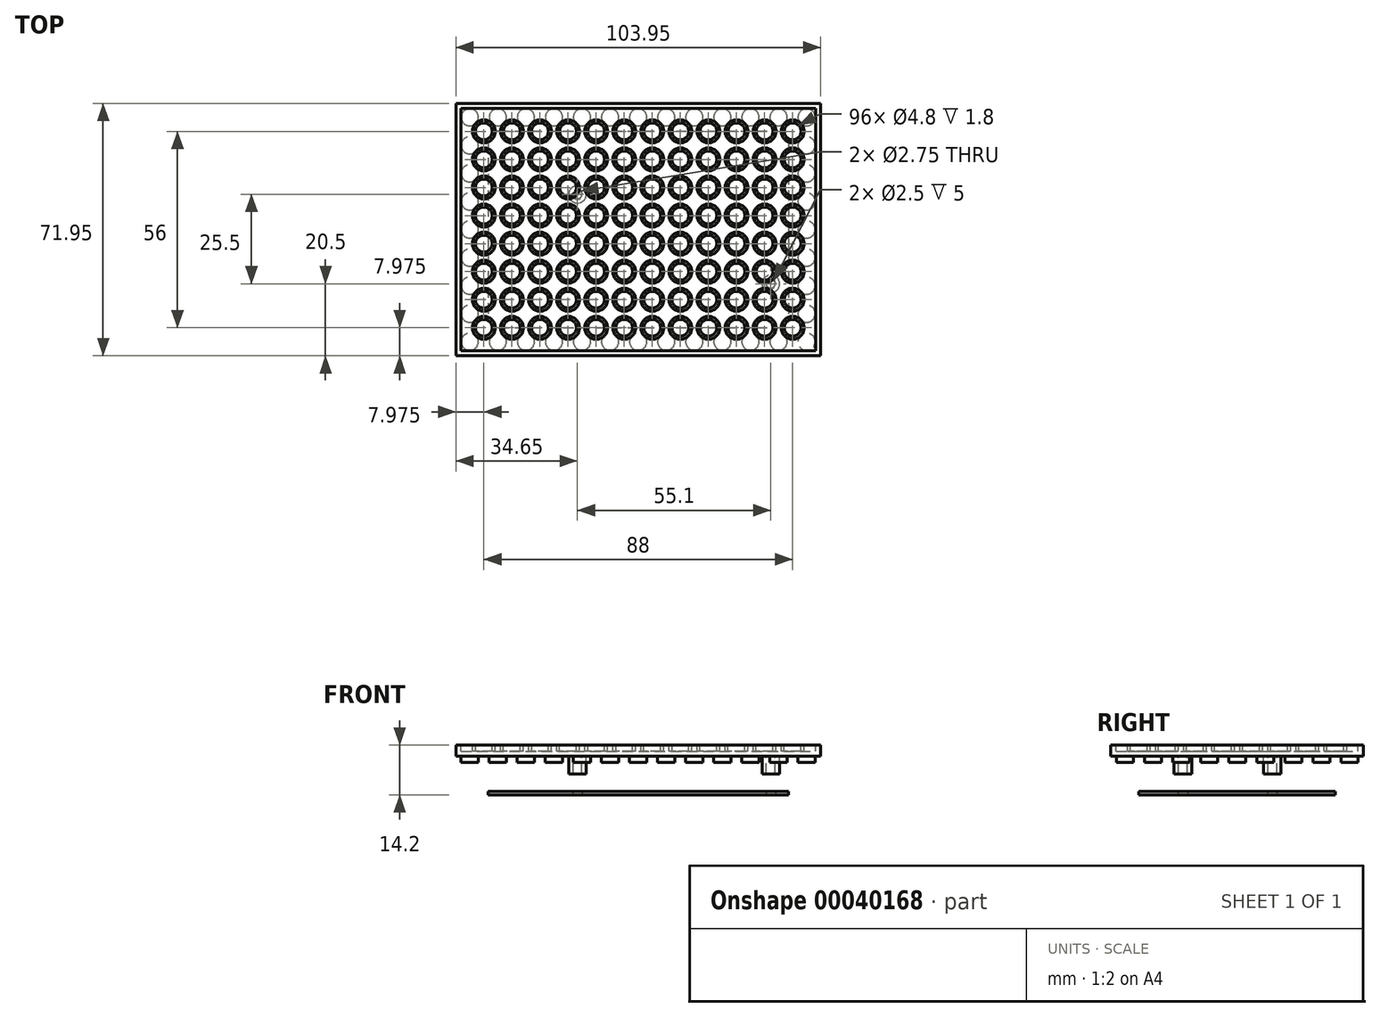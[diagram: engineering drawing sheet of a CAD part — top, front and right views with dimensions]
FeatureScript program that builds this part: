
annotation { "Feature Type Name" : "Feature", "Feature Type Description" : "" }
export const myFeature = defineFeature(function(context is Context, id is Id, definition is map)
    precondition{}
    {
        {
            var Q0;
            Q0=qCreatedBy(makeId("Top.planeOp"),FACE);
            var sketch = newSketch(context, id + "F0", { "sketchPlane" : qUnion([Q0])});
            skLineSegment(sketch, "E0.bottom", {"start": v(0, 0) * mm, "end": v(-103.95, 0) * mm});
            skLineSegment(sketch, "E0.top", {"start": v(0, 71.95) * mm, "end": v(-103.95, 71.95) * mm});
            skLineSegment(sketch, "E0.left", {"start": v(0, 0) * mm, "end": v(0, 71.95) * mm});
            skLineSegment(sketch, "E0.right", {"start": v(-103.95, 0) * mm, "end": v(-103.95, 71.95) * mm});
            skSolve(sketch);
        }
        {
            var Q0;
            Q0=makeQuery(id+"F0.imprint","IMPRINT",FACE,{"disambiguationData":[TD([[makeQuery(id+"F0.imprint","IMPRINT",EDGE,{"derivedFrom":sQuery(id+"F0.wireOp",EDGE,"E0.bottom")}),-1.0]])]});
            extrude(context, id + "F1", {"entities" : qUnion([Q0]), "oppositeDirection" : true, "depth" : 3.2 * mm});
        }
        {
            var Q0;
            Q0=qCreatedBy(makeId("Top.planeOp"),FACE);
            var sketch = newSketch(context, id + "F2", { "sketchPlane" : qUnion([Q0])});
            skLineSegment(sketch, "E1.bottom", {"start": v(-102.47, 1.47) * mm, "end": v(-1.47, 1.48) * mm});
            skLineSegment(sketch, "E1.top", {"start": v(-102.48, 70.47) * mm, "end": v(-1.48, 70.47) * mm});
            skLineSegment(sketch, "E1.left", {"start": v(-102.47, 1.47) * mm, "end": v(-102.48, 70.47) * mm});
            skLineSegment(sketch, "E1.right", {"start": v(-1.47, 1.48) * mm, "end": v(-1.48, 70.47) * mm});
            skCircle(sketch, "E2", {"center": v(-7.97, 7.98) * mm, "radius": 3.25 * mm});
            skLineSegment(sketch, "E3", {"start": v(-7.97, 7.98) * mm, "end": v(-7.98, 45.54) * mm, "construction": true});
            skCircle(sketch, "E4.0.1.0", {"center": v(-7.97, 15.98) * mm, "radius": 3.25 * mm});
            skCircle(sketch, "E4.0.2.0", {"center": v(-7.97, 23.98) * mm, "radius": 3.25 * mm});
            skCircle(sketch, "E4.0.3.0", {"center": v(-7.97, 31.98) * mm, "radius": 3.25 * mm});
            skCircle(sketch, "E4.0.4.0", {"center": v(-7.97, 39.98) * mm, "radius": 3.25 * mm});
            skCircle(sketch, "E4.0.5.0", {"center": v(-7.97, 47.98) * mm, "radius": 3.25 * mm});
            skCircle(sketch, "E4.0.6.0", {"center": v(-7.97, 55.98) * mm, "radius": 3.25 * mm});
            skCircle(sketch, "E4.0.7.0", {"center": v(-7.97, 63.98) * mm, "radius": 3.25 * mm});
            skCircle(sketch, "E4.1.0.0", {"center": v(-15.97, 7.98) * mm, "radius": 3.25 * mm});
            skCircle(sketch, "E4.1.1.0", {"center": v(-15.97, 15.98) * mm, "radius": 3.25 * mm});
            skCircle(sketch, "E4.1.2.0", {"center": v(-15.97, 23.98) * mm, "radius": 3.25 * mm});
            skCircle(sketch, "E4.1.3.0", {"center": v(-15.97, 31.98) * mm, "radius": 3.25 * mm});
            skCircle(sketch, "E4.1.4.0", {"center": v(-15.97, 39.98) * mm, "radius": 3.25 * mm});
            skCircle(sketch, "E4.1.5.0", {"center": v(-15.97, 47.98) * mm, "radius": 3.25 * mm});
            skCircle(sketch, "E4.1.6.0", {"center": v(-15.97, 55.98) * mm, "radius": 3.25 * mm});
            skCircle(sketch, "E4.1.7.0", {"center": v(-15.97, 63.98) * mm, "radius": 3.25 * mm});
            skCircle(sketch, "E4.2.0.0", {"center": v(-23.97, 7.98) * mm, "radius": 3.25 * mm});
            skCircle(sketch, "E4.2.1.0", {"center": v(-23.97, 15.98) * mm, "radius": 3.25 * mm});
            skCircle(sketch, "E4.2.2.0", {"center": v(-23.97, 23.98) * mm, "radius": 3.25 * mm});
            skCircle(sketch, "E4.2.3.0", {"center": v(-23.97, 31.98) * mm, "radius": 3.25 * mm});
            skCircle(sketch, "E4.2.4.0", {"center": v(-23.97, 39.98) * mm, "radius": 3.25 * mm});
            skCircle(sketch, "E4.2.5.0", {"center": v(-23.97, 47.98) * mm, "radius": 3.25 * mm});
            skCircle(sketch, "E4.2.6.0", {"center": v(-23.97, 55.98) * mm, "radius": 3.25 * mm});
            skCircle(sketch, "E4.2.7.0", {"center": v(-23.97, 63.98) * mm, "radius": 3.25 * mm});
            skCircle(sketch, "E4.3.0.0", {"center": v(-31.97, 7.98) * mm, "radius": 3.25 * mm});
            skCircle(sketch, "E4.3.1.0", {"center": v(-31.97, 15.98) * mm, "radius": 3.25 * mm});
            skCircle(sketch, "E4.3.2.0", {"center": v(-31.97, 23.98) * mm, "radius": 3.25 * mm});
            skCircle(sketch, "E4.3.3.0", {"center": v(-31.97, 31.98) * mm, "radius": 3.25 * mm});
            skCircle(sketch, "E4.3.4.0", {"center": v(-31.97, 39.98) * mm, "radius": 3.25 * mm});
            skCircle(sketch, "E4.3.5.0", {"center": v(-31.97, 47.98) * mm, "radius": 3.25 * mm});
            skCircle(sketch, "E4.3.6.0", {"center": v(-31.97, 55.98) * mm, "radius": 3.25 * mm});
            skCircle(sketch, "E4.3.7.0", {"center": v(-31.97, 63.98) * mm, "radius": 3.25 * mm});
            skCircle(sketch, "E4.4.0.0", {"center": v(-39.97, 7.98) * mm, "radius": 3.25 * mm});
            skCircle(sketch, "E4.4.1.0", {"center": v(-39.97, 15.98) * mm, "radius": 3.25 * mm});
            skCircle(sketch, "E4.4.2.0", {"center": v(-39.97, 23.98) * mm, "radius": 3.25 * mm});
            skCircle(sketch, "E4.4.3.0", {"center": v(-39.97, 31.98) * mm, "radius": 3.25 * mm});
            skCircle(sketch, "E4.4.4.0", {"center": v(-39.97, 39.98) * mm, "radius": 3.25 * mm});
            skCircle(sketch, "E4.4.5.0", {"center": v(-39.97, 47.98) * mm, "radius": 3.25 * mm});
            skCircle(sketch, "E4.4.6.0", {"center": v(-39.97, 55.98) * mm, "radius": 3.25 * mm});
            skCircle(sketch, "E4.4.7.0", {"center": v(-39.97, 63.98) * mm, "radius": 3.25 * mm});
            skCircle(sketch, "E4.5.0.0", {"center": v(-47.97, 7.98) * mm, "radius": 3.25 * mm});
            skCircle(sketch, "E4.5.1.0", {"center": v(-47.97, 15.98) * mm, "radius": 3.25 * mm});
            skCircle(sketch, "E4.5.2.0", {"center": v(-47.97, 23.98) * mm, "radius": 3.25 * mm});
            skCircle(sketch, "E4.5.3.0", {"center": v(-47.97, 31.98) * mm, "radius": 3.25 * mm});
            skCircle(sketch, "E4.5.4.0", {"center": v(-47.97, 39.98) * mm, "radius": 3.25 * mm});
            skCircle(sketch, "E4.5.5.0", {"center": v(-47.97, 47.98) * mm, "radius": 3.25 * mm});
            skCircle(sketch, "E4.5.6.0", {"center": v(-47.97, 55.98) * mm, "radius": 3.25 * mm});
            skCircle(sketch, "E4.5.7.0", {"center": v(-47.97, 63.98) * mm, "radius": 3.25 * mm});
            skCircle(sketch, "E4.6.0.0", {"center": v(-55.97, 7.98) * mm, "radius": 3.25 * mm});
            skCircle(sketch, "E4.6.1.0", {"center": v(-55.97, 15.98) * mm, "radius": 3.25 * mm});
            skCircle(sketch, "E4.6.2.0", {"center": v(-55.97, 23.98) * mm, "radius": 3.25 * mm});
            skCircle(sketch, "E4.6.3.0", {"center": v(-55.97, 31.98) * mm, "radius": 3.25 * mm});
            skCircle(sketch, "E4.6.4.0", {"center": v(-55.97, 39.98) * mm, "radius": 3.25 * mm});
            skCircle(sketch, "E4.6.5.0", {"center": v(-55.97, 47.98) * mm, "radius": 3.25 * mm});
            skCircle(sketch, "E4.6.6.0", {"center": v(-55.97, 55.98) * mm, "radius": 3.25 * mm});
            skCircle(sketch, "E4.6.7.0", {"center": v(-55.97, 63.98) * mm, "radius": 3.25 * mm});
            skCircle(sketch, "E4.7.0.0", {"center": v(-63.98, 7.98) * mm, "radius": 3.25 * mm});
            skCircle(sketch, "E4.7.1.0", {"center": v(-63.98, 15.98) * mm, "radius": 3.25 * mm});
            skCircle(sketch, "E4.7.2.0", {"center": v(-63.98, 23.98) * mm, "radius": 3.25 * mm});
            skCircle(sketch, "E4.7.3.0", {"center": v(-63.98, 31.98) * mm, "radius": 3.25 * mm});
            skCircle(sketch, "E4.7.4.0", {"center": v(-63.98, 39.98) * mm, "radius": 3.25 * mm});
            skCircle(sketch, "E4.7.5.0", {"center": v(-63.98, 47.98) * mm, "radius": 3.25 * mm});
            skCircle(sketch, "E4.7.6.0", {"center": v(-63.98, 55.98) * mm, "radius": 3.25 * mm});
            skCircle(sketch, "E4.7.7.0", {"center": v(-63.98, 63.98) * mm, "radius": 3.25 * mm});
            skCircle(sketch, "E4.8.0.0", {"center": v(-71.97, 7.98) * mm, "radius": 3.25 * mm});
            skCircle(sketch, "E4.8.1.0", {"center": v(-71.97, 15.98) * mm, "radius": 3.25 * mm});
            skCircle(sketch, "E4.8.2.0", {"center": v(-71.97, 23.98) * mm, "radius": 3.25 * mm});
            skCircle(sketch, "E4.8.3.0", {"center": v(-71.97, 31.98) * mm, "radius": 3.25 * mm});
            skCircle(sketch, "E4.8.4.0", {"center": v(-71.97, 39.98) * mm, "radius": 3.25 * mm});
            skCircle(sketch, "E4.8.5.0", {"center": v(-71.97, 47.98) * mm, "radius": 3.25 * mm});
            skCircle(sketch, "E4.8.6.0", {"center": v(-71.97, 55.98) * mm, "radius": 3.25 * mm});
            skCircle(sketch, "E4.8.7.0", {"center": v(-71.97, 63.98) * mm, "radius": 3.25 * mm});
            skCircle(sketch, "E4.9.0.0", {"center": v(-79.98, 7.98) * mm, "radius": 3.25 * mm});
            skCircle(sketch, "E4.9.1.0", {"center": v(-79.98, 15.98) * mm, "radius": 3.25 * mm});
            skCircle(sketch, "E4.9.2.0", {"center": v(-79.98, 23.98) * mm, "radius": 3.25 * mm});
            skCircle(sketch, "E4.9.3.0", {"center": v(-79.98, 31.98) * mm, "radius": 3.25 * mm});
            skCircle(sketch, "E4.9.4.0", {"center": v(-79.98, 39.98) * mm, "radius": 3.25 * mm});
            skCircle(sketch, "E4.9.5.0", {"center": v(-79.98, 47.98) * mm, "radius": 3.25 * mm});
            skCircle(sketch, "E4.9.6.0", {"center": v(-79.98, 55.98) * mm, "radius": 3.25 * mm});
            skCircle(sketch, "E4.9.7.0", {"center": v(-79.98, 63.98) * mm, "radius": 3.25 * mm});
            skCircle(sketch, "E4.10.0.0", {"center": v(-87.97, 7.98) * mm, "radius": 3.25 * mm});
            skCircle(sketch, "E4.10.1.0", {"center": v(-87.97, 15.98) * mm, "radius": 3.25 * mm});
            skCircle(sketch, "E4.10.2.0", {"center": v(-87.97, 23.98) * mm, "radius": 3.25 * mm});
            skCircle(sketch, "E4.10.3.0", {"center": v(-87.97, 31.98) * mm, "radius": 3.25 * mm});
            skCircle(sketch, "E4.10.4.0", {"center": v(-87.97, 39.98) * mm, "radius": 3.25 * mm});
            skCircle(sketch, "E4.10.5.0", {"center": v(-87.97, 47.98) * mm, "radius": 3.25 * mm});
            skCircle(sketch, "E4.10.6.0", {"center": v(-87.97, 55.98) * mm, "radius": 3.25 * mm});
            skCircle(sketch, "E4.10.7.0", {"center": v(-87.97, 63.98) * mm, "radius": 3.25 * mm});
            skCircle(sketch, "E4.11.0.0", {"center": v(-95.97, 7.98) * mm, "radius": 3.25 * mm});
            skCircle(sketch, "E4.11.1.0", {"center": v(-95.97, 15.98) * mm, "radius": 3.25 * mm});
            skCircle(sketch, "E4.11.2.0", {"center": v(-95.97, 23.98) * mm, "radius": 3.25 * mm});
            skCircle(sketch, "E4.11.3.0", {"center": v(-95.97, 31.98) * mm, "radius": 3.25 * mm});
            skCircle(sketch, "E4.11.4.0", {"center": v(-95.97, 39.98) * mm, "radius": 3.25 * mm});
            skCircle(sketch, "E4.11.5.0", {"center": v(-95.97, 47.98) * mm, "radius": 3.25 * mm});
            skCircle(sketch, "E4.11.6.0", {"center": v(-95.97, 55.98) * mm, "radius": 3.25 * mm});
            skCircle(sketch, "E4.11.7.0", {"center": v(-95.97, 63.98) * mm, "radius": 3.25 * mm});
            skLineSegment(sketch, "E4.direction1", {"start": v(-7.97, 7.98) * mm, "end": v(-15.97, 7.98) * mm, "construction": true});
            skLineSegment(sketch, "E4.direction2", {"start": v(-7.97, 7.98) * mm, "end": v(-7.97, 15.98) * mm, "construction": true});
            skSolve(sketch);
        }
        {
            var Q0;
            Q0=qCreatedBy(makeId("Top.planeOp"),FACE);
            var sketch = newSketch(context, id + "F3", { "sketchPlane" : qUnion([Q0])});
            skCircle(sketch, "E5", {"center": v(-7.97, 7.97) * mm, "radius": 2.4 * mm});
            skLineSegment(sketch, "E6", {"start": v(-7.97, 7.97) * mm, "end": v(-7.97, 10.16) * mm, "construction": true});
            skCircle(sketch, "E7.0.1.0", {"center": v(-7.97, 15.97) * mm, "radius": 2.4 * mm});
            skCircle(sketch, "E7.0.2.0", {"center": v(-7.97, 23.97) * mm, "radius": 2.4 * mm});
            skCircle(sketch, "E7.0.3.0", {"center": v(-7.97, 31.97) * mm, "radius": 2.4 * mm});
            skCircle(sketch, "E7.0.4.0", {"center": v(-7.97, 39.97) * mm, "radius": 2.4 * mm});
            skCircle(sketch, "E7.0.5.0", {"center": v(-7.97, 47.97) * mm, "radius": 2.4 * mm});
            skCircle(sketch, "E7.0.6.0", {"center": v(-7.97, 55.97) * mm, "radius": 2.4 * mm});
            skCircle(sketch, "E7.0.7.0", {"center": v(-7.97, 63.97) * mm, "radius": 2.4 * mm});
            skCircle(sketch, "E7.1.0.0", {"center": v(-15.97, 7.97) * mm, "radius": 2.4 * mm});
            skCircle(sketch, "E7.1.1.0", {"center": v(-15.97, 15.97) * mm, "radius": 2.4 * mm});
            skCircle(sketch, "E7.1.2.0", {"center": v(-15.97, 23.97) * mm, "radius": 2.4 * mm});
            skCircle(sketch, "E7.1.3.0", {"center": v(-15.97, 31.97) * mm, "radius": 2.4 * mm});
            skCircle(sketch, "E7.1.4.0", {"center": v(-15.97, 39.97) * mm, "radius": 2.4 * mm});
            skCircle(sketch, "E7.1.5.0", {"center": v(-15.97, 47.97) * mm, "radius": 2.4 * mm});
            skCircle(sketch, "E7.1.6.0", {"center": v(-15.97, 55.97) * mm, "radius": 2.4 * mm});
            skCircle(sketch, "E7.1.7.0", {"center": v(-15.97, 63.97) * mm, "radius": 2.4 * mm});
            skCircle(sketch, "E7.2.0.0", {"center": v(-23.97, 7.97) * mm, "radius": 2.4 * mm});
            skCircle(sketch, "E7.2.1.0", {"center": v(-23.97, 15.97) * mm, "radius": 2.4 * mm});
            skCircle(sketch, "E7.2.2.0", {"center": v(-23.97, 23.97) * mm, "radius": 2.4 * mm});
            skCircle(sketch, "E7.2.3.0", {"center": v(-23.97, 31.97) * mm, "radius": 2.4 * mm});
            skCircle(sketch, "E7.2.4.0", {"center": v(-23.97, 39.97) * mm, "radius": 2.4 * mm});
            skCircle(sketch, "E7.2.5.0", {"center": v(-23.97, 47.97) * mm, "radius": 2.4 * mm});
            skCircle(sketch, "E7.2.6.0", {"center": v(-23.97, 55.97) * mm, "radius": 2.4 * mm});
            skCircle(sketch, "E7.2.7.0", {"center": v(-23.97, 63.97) * mm, "radius": 2.4 * mm});
            skCircle(sketch, "E7.3.0.0", {"center": v(-31.97, 7.97) * mm, "radius": 2.4 * mm});
            skCircle(sketch, "E7.3.1.0", {"center": v(-31.97, 15.97) * mm, "radius": 2.4 * mm});
            skCircle(sketch, "E7.3.2.0", {"center": v(-31.97, 23.97) * mm, "radius": 2.4 * mm});
            skCircle(sketch, "E7.3.3.0", {"center": v(-31.97, 31.97) * mm, "radius": 2.4 * mm});
            skCircle(sketch, "E7.3.4.0", {"center": v(-31.97, 39.97) * mm, "radius": 2.4 * mm});
            skCircle(sketch, "E7.3.5.0", {"center": v(-31.97, 47.97) * mm, "radius": 2.4 * mm});
            skCircle(sketch, "E7.3.6.0", {"center": v(-31.97, 55.97) * mm, "radius": 2.4 * mm});
            skCircle(sketch, "E7.3.7.0", {"center": v(-31.97, 63.97) * mm, "radius": 2.4 * mm});
            skCircle(sketch, "E7.4.0.0", {"center": v(-39.97, 7.97) * mm, "radius": 2.4 * mm});
            skCircle(sketch, "E7.4.1.0", {"center": v(-39.97, 15.97) * mm, "radius": 2.4 * mm});
            skCircle(sketch, "E7.4.2.0", {"center": v(-39.97, 23.97) * mm, "radius": 2.4 * mm});
            skCircle(sketch, "E7.4.3.0", {"center": v(-39.97, 31.97) * mm, "radius": 2.4 * mm});
            skCircle(sketch, "E7.4.4.0", {"center": v(-39.97, 39.97) * mm, "radius": 2.4 * mm});
            skCircle(sketch, "E7.4.5.0", {"center": v(-39.97, 47.97) * mm, "radius": 2.4 * mm});
            skCircle(sketch, "E7.4.6.0", {"center": v(-39.97, 55.97) * mm, "radius": 2.4 * mm});
            skCircle(sketch, "E7.4.7.0", {"center": v(-39.97, 63.97) * mm, "radius": 2.4 * mm});
            skCircle(sketch, "E7.5.0.0", {"center": v(-47.97, 7.97) * mm, "radius": 2.4 * mm});
            skCircle(sketch, "E7.5.1.0", {"center": v(-47.97, 15.97) * mm, "radius": 2.4 * mm});
            skCircle(sketch, "E7.5.2.0", {"center": v(-47.97, 23.97) * mm, "radius": 2.4 * mm});
            skCircle(sketch, "E7.5.3.0", {"center": v(-47.97, 31.97) * mm, "radius": 2.4 * mm});
            skCircle(sketch, "E7.5.4.0", {"center": v(-47.97, 39.97) * mm, "radius": 2.4 * mm});
            skCircle(sketch, "E7.5.5.0", {"center": v(-47.97, 47.97) * mm, "radius": 2.4 * mm});
            skCircle(sketch, "E7.5.6.0", {"center": v(-47.97, 55.97) * mm, "radius": 2.4 * mm});
            skCircle(sketch, "E7.5.7.0", {"center": v(-47.97, 63.97) * mm, "radius": 2.4 * mm});
            skCircle(sketch, "E7.6.0.0", {"center": v(-55.97, 7.97) * mm, "radius": 2.4 * mm});
            skCircle(sketch, "E7.6.1.0", {"center": v(-55.97, 15.97) * mm, "radius": 2.4 * mm});
            skCircle(sketch, "E7.6.2.0", {"center": v(-55.97, 23.97) * mm, "radius": 2.4 * mm});
            skCircle(sketch, "E7.6.3.0", {"center": v(-55.97, 31.97) * mm, "radius": 2.4 * mm});
            skCircle(sketch, "E7.6.4.0", {"center": v(-55.97, 39.97) * mm, "radius": 2.4 * mm});
            skCircle(sketch, "E7.6.5.0", {"center": v(-55.97, 47.97) * mm, "radius": 2.4 * mm});
            skCircle(sketch, "E7.6.6.0", {"center": v(-55.97, 55.97) * mm, "radius": 2.4 * mm});
            skCircle(sketch, "E7.6.7.0", {"center": v(-55.97, 63.97) * mm, "radius": 2.4 * mm});
            skCircle(sketch, "E7.7.0.0", {"center": v(-63.97, 7.97) * mm, "radius": 2.4 * mm});
            skCircle(sketch, "E7.7.1.0", {"center": v(-63.97, 15.97) * mm, "radius": 2.4 * mm});
            skCircle(sketch, "E7.7.2.0", {"center": v(-63.97, 23.97) * mm, "radius": 2.4 * mm});
            skCircle(sketch, "E7.7.3.0", {"center": v(-63.97, 31.97) * mm, "radius": 2.4 * mm});
            skCircle(sketch, "E7.7.4.0", {"center": v(-63.97, 39.97) * mm, "radius": 2.4 * mm});
            skCircle(sketch, "E7.7.5.0", {"center": v(-63.97, 47.97) * mm, "radius": 2.4 * mm});
            skCircle(sketch, "E7.7.6.0", {"center": v(-63.97, 55.97) * mm, "radius": 2.4 * mm});
            skCircle(sketch, "E7.7.7.0", {"center": v(-63.97, 63.97) * mm, "radius": 2.4 * mm});
            skCircle(sketch, "E7.8.0.0", {"center": v(-71.97, 7.97) * mm, "radius": 2.4 * mm});
            skCircle(sketch, "E7.8.1.0", {"center": v(-71.97, 15.97) * mm, "radius": 2.4 * mm});
            skCircle(sketch, "E7.8.2.0", {"center": v(-71.97, 23.97) * mm, "radius": 2.4 * mm});
            skCircle(sketch, "E7.8.3.0", {"center": v(-71.97, 31.97) * mm, "radius": 2.4 * mm});
            skCircle(sketch, "E7.8.4.0", {"center": v(-71.97, 39.97) * mm, "radius": 2.4 * mm});
            skCircle(sketch, "E7.8.5.0", {"center": v(-71.97, 47.97) * mm, "radius": 2.4 * mm});
            skCircle(sketch, "E7.8.6.0", {"center": v(-71.97, 55.97) * mm, "radius": 2.4 * mm});
            skCircle(sketch, "E7.8.7.0", {"center": v(-71.97, 63.97) * mm, "radius": 2.4 * mm});
            skCircle(sketch, "E7.9.0.0", {"center": v(-79.97, 7.97) * mm, "radius": 2.4 * mm});
            skCircle(sketch, "E7.9.1.0", {"center": v(-79.97, 15.97) * mm, "radius": 2.4 * mm});
            skCircle(sketch, "E7.9.2.0", {"center": v(-79.97, 23.97) * mm, "radius": 2.4 * mm});
            skCircle(sketch, "E7.9.3.0", {"center": v(-79.97, 31.97) * mm, "radius": 2.4 * mm});
            skCircle(sketch, "E7.9.4.0", {"center": v(-79.97, 39.97) * mm, "radius": 2.4 * mm});
            skCircle(sketch, "E7.9.5.0", {"center": v(-79.97, 47.97) * mm, "radius": 2.4 * mm});
            skCircle(sketch, "E7.9.6.0", {"center": v(-79.97, 55.97) * mm, "radius": 2.4 * mm});
            skCircle(sketch, "E7.9.7.0", {"center": v(-79.97, 63.97) * mm, "radius": 2.4 * mm});
            skCircle(sketch, "E7.10.0.0", {"center": v(-87.97, 7.97) * mm, "radius": 2.4 * mm});
            skCircle(sketch, "E7.10.1.0", {"center": v(-87.97, 15.97) * mm, "radius": 2.4 * mm});
            skCircle(sketch, "E7.10.2.0", {"center": v(-87.97, 23.97) * mm, "radius": 2.4 * mm});
            skCircle(sketch, "E7.10.3.0", {"center": v(-87.97, 31.97) * mm, "radius": 2.4 * mm});
            skCircle(sketch, "E7.10.4.0", {"center": v(-87.97, 39.97) * mm, "radius": 2.4 * mm});
            skCircle(sketch, "E7.10.5.0", {"center": v(-87.97, 47.97) * mm, "radius": 2.4 * mm});
            skCircle(sketch, "E7.10.6.0", {"center": v(-87.97, 55.97) * mm, "radius": 2.4 * mm});
            skCircle(sketch, "E7.10.7.0", {"center": v(-87.97, 63.97) * mm, "radius": 2.4 * mm});
            skCircle(sketch, "E7.11.0.0", {"center": v(-95.97, 7.97) * mm, "radius": 2.4 * mm});
            skCircle(sketch, "E7.11.1.0", {"center": v(-95.97, 15.97) * mm, "radius": 2.4 * mm});
            skCircle(sketch, "E7.11.2.0", {"center": v(-95.97, 23.97) * mm, "radius": 2.4 * mm});
            skCircle(sketch, "E7.11.3.0", {"center": v(-95.97, 31.97) * mm, "radius": 2.4 * mm});
            skCircle(sketch, "E7.11.4.0", {"center": v(-95.97, 39.97) * mm, "radius": 2.4 * mm});
            skCircle(sketch, "E7.11.5.0", {"center": v(-95.97, 47.97) * mm, "radius": 2.4 * mm});
            skCircle(sketch, "E7.11.6.0", {"center": v(-95.97, 55.97) * mm, "radius": 2.4 * mm});
            skCircle(sketch, "E7.11.7.0", {"center": v(-95.97, 63.97) * mm, "radius": 2.4 * mm});
            skLineSegment(sketch, "E7.direction1", {"start": v(-7.97, 7.97) * mm, "end": v(-15.97, 7.97) * mm, "construction": true});
            skLineSegment(sketch, "E7.direction2", {"start": v(-7.97, 7.97) * mm, "end": v(-7.97, 15.97) * mm, "construction": true});
            skSolve(sketch);
        }
        {
            var Q0;
            Q0=qSketchRegion(id+"F2",true);
            var Q1;
            Q1=qSketchRegion(id+"F3",true);
            var Q2;
            Q2=sQuery(id+"F2.wireOp",EDGE,"de4b574f-d5fe-483e-a269-1c24a673af37.0.MirrorC");
            extrude(context, id + "F4", {"entities" : qUnion([Q0, Q1]), "operationType" : NewBodyOperationType.REMOVE, "surfaceEntities" : qUnion([Q2]), "oppositeDirection" : true, "depth" : 1.8 * mm});
        }
        {
            var Q0;
            Q0=makeQuery(id+"F1.opExtrude","CAP_FACE",FACE,{"disambiguationData":[OSD([sQuery(id+"F0.wireOp",EDGE,"E0.bottom"),sQuery(id+"F0.wireOp",EDGE,"E0.top"),sQuery(id+"F0.wireOp",EDGE,"E0.left"),sQuery(id+"F0.wireOp",EDGE,"E0.right")])],"isStart":false});
            var sketch = newSketch(context, id + "F5", { "sketchPlane" : qUnion([Q0])});
            skCircle(sketch, "E8", {"center": v(-4, -4) * mm, "radius": 2.45 * mm});
            skCircle(sketch, "E9.0.1.0", {"center": v(-4, -12) * mm, "radius": 2.45 * mm});
            skCircle(sketch, "E9.0.2.0", {"center": v(-4, -20) * mm, "radius": 2.45 * mm});
            skCircle(sketch, "E9.0.3.0", {"center": v(-4, -28) * mm, "radius": 2.45 * mm});
            skCircle(sketch, "E9.0.4.0", {"center": v(-4, -36) * mm, "radius": 2.45 * mm});
            skCircle(sketch, "E9.0.5.0", {"center": v(-4, -44) * mm, "radius": 2.45 * mm});
            skCircle(sketch, "E9.0.6.0", {"center": v(-4, -52) * mm, "radius": 2.45 * mm});
            skCircle(sketch, "E9.0.7.0", {"center": v(-4, -60) * mm, "radius": 2.45 * mm});
            skCircle(sketch, "E9.0.8.0", {"center": v(-4, -68) * mm, "radius": 2.45 * mm});
            skCircle(sketch, "E9.1.0.0", {"center": v(-100, -4) * mm, "radius": 2.45 * mm});
            skCircle(sketch, "E9.1.1.0", {"center": v(-100, -12) * mm, "radius": 2.45 * mm});
            skCircle(sketch, "E9.1.2.0", {"center": v(-100, -20) * mm, "radius": 2.45 * mm});
            skCircle(sketch, "E9.1.3.0", {"center": v(-100, -28) * mm, "radius": 2.45 * mm});
            skCircle(sketch, "E9.1.4.0", {"center": v(-100, -36) * mm, "radius": 2.45 * mm});
            skCircle(sketch, "E9.1.5.0", {"center": v(-100, -44) * mm, "radius": 2.45 * mm});
            skCircle(sketch, "E9.1.6.0", {"center": v(-100, -52) * mm, "radius": 2.45 * mm});
            skCircle(sketch, "E9.1.7.0", {"center": v(-100, -60) * mm, "radius": 2.45 * mm});
            skCircle(sketch, "E9.1.8.0", {"center": v(-100, -68) * mm, "radius": 2.45 * mm});
            skLineSegment(sketch, "E9.direction1", {"start": v(-4, -4) * mm, "end": v(-100, -4) * mm, "construction": true});
            skLineSegment(sketch, "E9.direction2", {"start": v(-4, -4) * mm, "end": v(-4, -12) * mm, "construction": true});
            skCircle(sketch, "E10.1.0.0", {"center": v(-12, -4) * mm, "radius": 2.45 * mm});
            skCircle(sketch, "E10.2.0.0", {"center": v(-20, -4) * mm, "radius": 2.45 * mm});
            skCircle(sketch, "E10.3.0.0", {"center": v(-28, -4) * mm, "radius": 2.45 * mm});
            skCircle(sketch, "E10.4.0.0", {"center": v(-36, -4) * mm, "radius": 2.45 * mm});
            skCircle(sketch, "E10.5.0.0", {"center": v(-44, -4) * mm, "radius": 2.45 * mm});
            skCircle(sketch, "E10.6.0.0", {"center": v(-52, -4) * mm, "radius": 2.45 * mm});
            skCircle(sketch, "E10.7.0.0", {"center": v(-60, -4) * mm, "radius": 2.45 * mm});
            skCircle(sketch, "E10.8.0.0", {"center": v(-68, -4) * mm, "radius": 2.45 * mm});
            skCircle(sketch, "E10.9.0.0", {"center": v(-76, -4) * mm, "radius": 2.45 * mm});
            skCircle(sketch, "E10.10.0.0", {"center": v(-84, -4) * mm, "radius": 2.45 * mm});
            skCircle(sketch, "E10.11.0.0", {"center": v(-92, -4) * mm, "radius": 2.45 * mm});
            skLineSegment(sketch, "E10.direction1", {"start": v(-4, -4) * mm, "end": v(-12, -4) * mm, "construction": true});
            skCircle(sketch, "E11.1.0.0", {"center": v(-12, -68) * mm, "radius": 2.45 * mm});
            skCircle(sketch, "E11.2.0.0", {"center": v(-20, -68) * mm, "radius": 2.45 * mm});
            skCircle(sketch, "E11.3.0.0", {"center": v(-28, -68) * mm, "radius": 2.45 * mm});
            skCircle(sketch, "E11.4.0.0", {"center": v(-36, -68) * mm, "radius": 2.45 * mm});
            skCircle(sketch, "E11.5.0.0", {"center": v(-44, -68) * mm, "radius": 2.45 * mm});
            skCircle(sketch, "E11.6.0.0", {"center": v(-52, -68) * mm, "radius": 2.45 * mm});
            skCircle(sketch, "E11.7.0.0", {"center": v(-60, -68) * mm, "radius": 2.45 * mm});
            skCircle(sketch, "E11.8.0.0", {"center": v(-68, -68) * mm, "radius": 2.45 * mm});
            skCircle(sketch, "E11.9.0.0", {"center": v(-76, -68) * mm, "radius": 2.45 * mm});
            skCircle(sketch, "E11.10.0.0", {"center": v(-84, -68) * mm, "radius": 2.45 * mm});
            skCircle(sketch, "E11.11.0.0", {"center": v(-92, -68) * mm, "radius": 2.45 * mm});
            skLineSegment(sketch, "E11.direction1", {"start": v(-4, -68) * mm, "end": v(-12, -68) * mm, "construction": true});
            skSolve(sketch);
        }
        {
            var Q0;
            Q0=qSketchRegion(id+"F5",true);
            extrude(context, id + "F6", {"entities" : qUnion([Q0]), "operationType" : NewBodyOperationType.ADD, "depth" : 1.7 * mm});
        }
        {
            var Q0;
            Q0=makeQuery(id+"F1.opExtrude","CAP_FACE",FACE,{"disambiguationData":[OSD([sQuery(id+"F0.wireOp",EDGE,"E0.bottom"),sQuery(id+"F0.wireOp",EDGE,"E0.top"),sQuery(id+"F0.wireOp",EDGE,"E0.left"),sQuery(id+"F0.wireOp",EDGE,"E0.right")])],"isStart":false});
            var sketch = newSketch(context, id + "F7", { "sketchPlane" : qUnion([Q0])});
            skCircle(sketch, "E12", {"center": v(-14.2, -20.5) * mm, "radius": 1.25 * mm});
            skCircle(sketch, "E13", {"center": v(-14.2, -20.5) * mm, "radius": 2.5 * mm});
            skCircle(sketch, "E14", {"center": v(-69.3, -46) * mm, "radius": 1.25 * mm});
            skCircle(sketch, "E15", {"center": v(-69.3, -46) * mm, "radius": 2.5 * mm});
            skSolve(sketch);
        }
        {
            var Q0;
            Q0=qSketchRegion(id+"F7",true);
            extrude(context, id + "F8", {"entities" : qUnion([Q0]), "operationType" : NewBodyOperationType.ADD, "depth" : 5 * mm});
        }
        {
            var Q0;
            Q0=makeQuery(id+"F8.opExtrude","CAP_FACE",FACE,{"disambiguationData":[OSD([sQuery(id+"F7.wireOp",EDGE,"E12"),sQuery(id+"F7.wireOp",EDGE,"E13")])],"isStart":false});
            cPlane(context, id + "F9", {"entities" : qUnion([Q0]), "cplaneType" : CPlaneType.OFFSET, "offset" : 5 * mm, "width" : 150 * mm, "height" : 150 * mm});
        }
        {
            var Q0;
            Q0=qCreatedBy(id+"F9.planeOp",FACE);
            var sketch = newSketch(context, id + "F10", { "sketchPlane" : qUnion([Q0])});
            skLineSegment(sketch, "E16.bottom", {"start": v(-94.8, -64) * mm, "end": v(-9.2, -64) * mm});
            skLineSegment(sketch, "E16.top", {"start": v(-94.8, -8) * mm, "end": v(-9.2, -8) * mm});
            skLineSegment(sketch, "E16.left", {"start": v(-94.8, -64) * mm, "end": v(-94.8, -8) * mm});
            skLineSegment(sketch, "E16.right", {"start": v(-9.2, -64) * mm, "end": v(-9.2, -8) * mm});
            skSolve(sketch);
        }
        {
            var Q0;
            Q0=qSketchRegion(id+"F10",true);
            extrude(context, id + "F11", {"entities" : qUnion([Q0]), "depth" : 1 * mm});
        }
        {
            var Q0;
            Q0=makeQuery(id+"F11.opExtrude","SWEPT_EDGE",EDGE,{"disambiguationData":[OSD([sQuery(id+"F10.wireOp",EDGE,"E16.top"),sQuery(id+"F10.wireOp",EDGE,"E16.left")])]});
            var Q1;
            Q1=makeQuery(id+"F11.opExtrude","SWEPT_EDGE",EDGE,{"disambiguationData":[OSD([sQuery(id+"F10.wireOp",EDGE,"E16.bottom"),sQuery(id+"F10.wireOp",EDGE,"E16.left")])]});
            var Q2;
            Q2=makeQuery(id+"F11.opExtrude","SWEPT_EDGE",EDGE,{"disambiguationData":[OSD([sQuery(id+"F10.wireOp",EDGE,"E16.bottom"),sQuery(id+"F10.wireOp",EDGE,"E16.right")])]});
            var Q3;
            Q3=makeQuery(id+"F11.opExtrude","SWEPT_EDGE",EDGE,{"disambiguationData":[OSD([sQuery(id+"F10.wireOp",EDGE,"E16.top"),sQuery(id+"F10.wireOp",EDGE,"E16.right")])]});
            fillet(context, id + "F12", {"entities" : qUnion([Q0, Q1, Q2, Q3]), "radius" : 3 * mm, "allowEdgeOverflow" : false});
        }
        {
            var Q0;
            Q0=makeQuery(id+"F11.opExtrude","CAP_FACE",FACE,{"disambiguationData":[OSD([sQuery(id+"F10.wireOp",EDGE,"E16.bottom"),sQuery(id+"F10.wireOp",EDGE,"E16.top"),sQuery(id+"F10.wireOp",EDGE,"E16.left"),sQuery(id+"F10.wireOp",EDGE,"E16.right")])],"isStart":false});
            var sketch = newSketch(context, id + "F13", { "sketchPlane" : qUnion([Q0])});
            skCircle(sketch, "E17", {"center": v(-14.2, -20.5) * mm, "radius": 1.38 * mm});
            skCircle(sketch, "E18.0.1.0", {"center": v(-69.3, -46) * mm, "radius": 1.38 * mm});
            skSolve(sketch);
        }
        {
            var Q0;
            Q0=qSketchRegion(id+"F13",true);
            var Q1;
            Q1=makeQuery(id+"F11.opExtrude","CAP_FACE",FACE,{"disambiguationData":[OSD([sQuery(id+"F10.wireOp",EDGE,"E16.bottom"),sQuery(id+"F10.wireOp",EDGE,"E16.top"),sQuery(id+"F10.wireOp",EDGE,"E16.left"),sQuery(id+"F10.wireOp",EDGE,"E16.right")])],"isStart":true});
            extrude(context, id + "F14", {"entities" : qUnion([Q0]), "operationType" : NewBodyOperationType.REMOVE, "endBound" : BoundingType.UP_TO_SURFACE, "oppositeDirection" : true, "endBoundEntityFace" : qUnion([Q1]), "depth" : 25 * mm});
        }
    });
